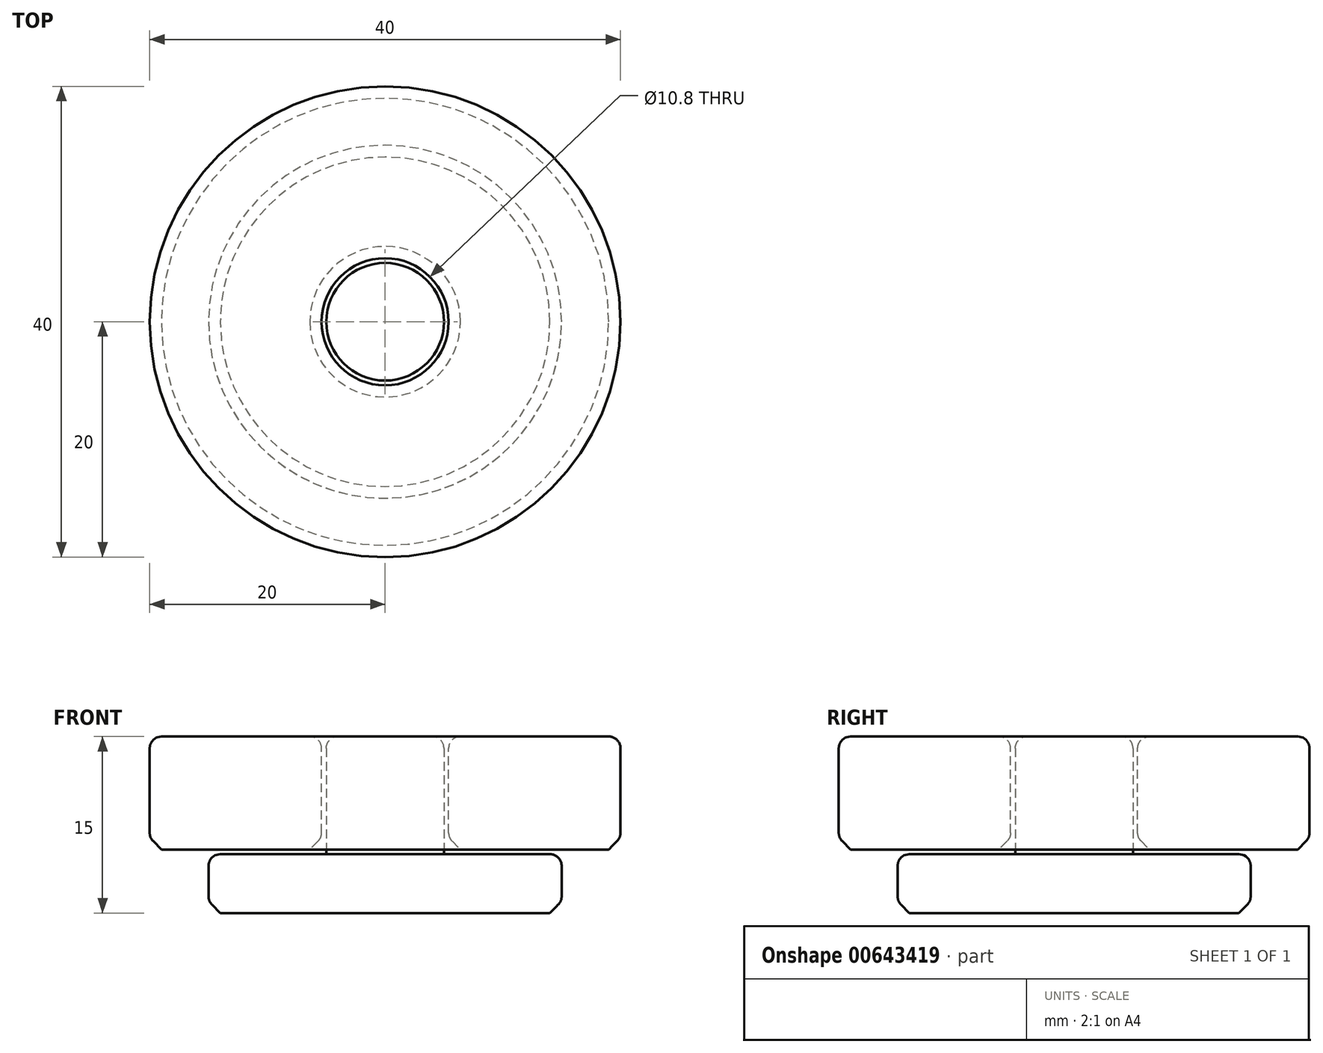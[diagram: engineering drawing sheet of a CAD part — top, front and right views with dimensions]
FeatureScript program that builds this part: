
annotation { "Feature Type Name" : "Feature", "Feature Type Description" : "" }
export const myFeature = defineFeature(function(context is Context, id is Id, definition is map)
    precondition{}
    {
        {
            assignVariable(context, id + "F0", {"name" : "tollerance", "anyValue" : 0.4});
        }
        {
            var Q0;
            Q0=qCreatedBy(makeId("Top.planeOp"),FACE);
            var sketch = newSketch(context, id + "F1", { "sketchPlane" : qUnion([Q0])});
            skCircle(sketch, "E0", {"center": v(0, 0) * mm, "radius": 15 * mm});
            skCircle(sketch, "E1", {"center": v(0, 0) * mm, "radius": 5 * mm});
            skSolve(sketch);
        }
        {
            var Q0;
            Q0=makeQuery(id+"F1.imprint","IMPRINT",FACE,{"disambiguationData":[TD([[makeQuery(id+"F1.imprint","IMPRINT",EDGE,{"derivedFrom":sQuery(id+"F1.wireOp",EDGE,"E0")}),1.0]])]});
            var Q1;
            Q1=makeQuery(id+"F1.imprint","IMPRINT",FACE,{"disambiguationData":[TD([[makeQuery(id+"F1.imprint","IMPRINT",EDGE,{"derivedFrom":sQuery(id+"F1.wireOp",EDGE,"E1")}),1.0]])]});
            extrude(context, id + "F2", {"entities" : qUnion([Q0, Q1]), "depth" : 5 * mm, "offsetDistance" : 25 * mm});
        }
        {
            var Q0;
            Q0=makeQuery(id+"F1.imprint","IMPRINT",FACE,{"disambiguationData":[TD([[makeQuery(id+"F1.imprint","IMPRINT",EDGE,{"derivedFrom":sQuery(id+"F1.wireOp",EDGE,"E1")}),1.0]])]});
            extrude(context, id + "F3", {"entities" : qUnion([Q0]), "operationType" : NewBodyOperationType.ADD, "depth" : 15 * mm, "offsetDistance" : 25 * mm});
        }
        {
            var Q0;
            Q0=makeQuery(id+"F3.opExtrude","CAP_FACE",FACE,{"disambiguationData":[OSD([sQuery(id+"F1.wireOp",EDGE,"E1")])],"isStart":false});
            var sketch = newSketch(context, id + "F4", { "sketchPlane" : qUnion([Q0])});
            skCircle(sketch, "E2.0", {"center": v(0, 0) * mm, "radius": 5.4 * mm});
            skCircle(sketch, "E3.0", {"center": v(0, 0) * mm, "radius": 20 * mm});
            skSolve(sketch);
        }
        {
            var Q0;
            Q0 = qSketchRegion(id + "F4", true);
            extrude(context, id + "F5", {"entities" : qUnion([Q0]), "oppositeDirection" : true, "depth" : (10 - getVariable(context, 'tollerance')) * mm, "offsetDistance" : 25 * mm});
        }
        {
            var Q0;
            Q0=makeQuery(id+"F5.opExtrude","CAP_FACE",FACE,{"disambiguationData":[OSD([sQuery(id+"F4.wireOp",EDGE,"E2.0"),sQuery(id+"F4.wireOp",EDGE,"E3.0")])],"isStart":false});
            chamfer(context, id + "F6", {"entities" : qUnion([Q0]), "width" : 1 * mm, "tangentPropagation" : true});
        }
        {
            var Q0;
            Q0=makeQuery(id+"F5.opExtrude","SWEPT_FACE",FACE,{"disambiguationData":[OSD([sQuery(id+"F4.wireOp",EDGE,"E3.0")])]});
            var Q1;
            Q1=makeQuery(id+"F5.opExtrude","SWEPT_FACE",FACE,{"disambiguationData":[OSD([sQuery(id+"F4.wireOp",EDGE,"E2.0")])]});
            fillet(context, id + "F7", {"entities" : qUnion([Q0, Q1]), "radius" : 1 * mm, "tangentPropagation" : true, "allowEdgeOverflow" : false});
        }
        {
            var Q0;
            Q0=makeQuery(id+"F2.opExtrude","CAP_FACE",FACE,{"disambiguationData":[OSD([sQuery(id+"F1.wireOp",EDGE,"E0")])],"isStart":true});
            chamfer(context, id + "F8", {"entities" : qUnion([Q0]), "width" : 1 * mm, "tangentPropagation" : true});
        }
        {
            var Q0;
            Q0=makeQuery(id+"F2.opExtrude","SWEPT_FACE",FACE,{"disambiguationData":[OSD([sQuery(id+"F1.wireOp",EDGE,"E0")])]});
            var Q1;
            Q1=makeQuery(id+"F3.opExtrude","CAP_EDGE",EDGE,{"disambiguationData":[OSD([sQuery(id+"F1.wireOp",EDGE,"E1")])],"isStart":false});
            fillet(context, id + "F9", {"entities" : qUnion([Q0, Q1]), "radius" : 1 * mm, "tangentPropagation" : true, "allowEdgeOverflow" : false});
        }
    });
